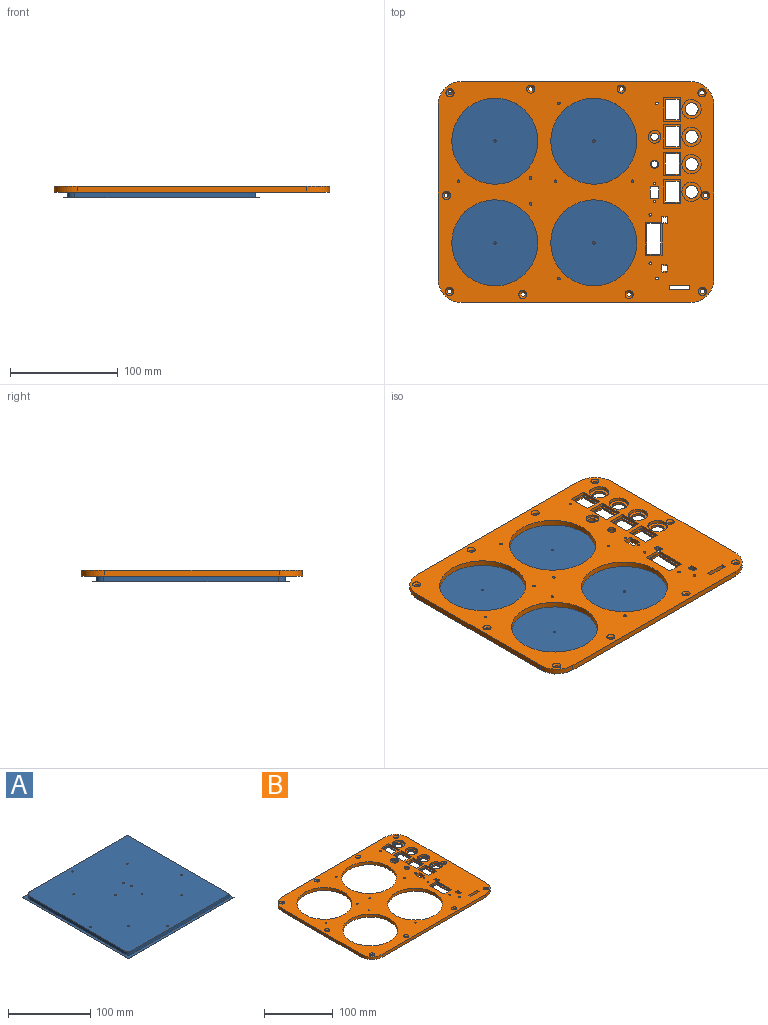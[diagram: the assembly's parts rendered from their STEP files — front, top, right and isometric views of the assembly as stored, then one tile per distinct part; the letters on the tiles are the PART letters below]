
ASSEMBLY  parts=2 mates=1
PART A: 37 faces, bbox 182.3x183x5.2 mm
  f0: plane 168.95x5.1mm, normal (0,1,0), area 861.6mm2, adj f2,f17,f18,f19
  f1: plane 163.3x5.1mm, normal (-1,0,0), area 832.8mm2, adj f16,f17,f18,f19
  f2: plane 176x5.1mm, normal (1,0,0), area 897.6mm2, adj f0,f15,f18,f19
  f3: cylinder r=1.19mm len=5.1mm, axis (0,0,1), area 38.2mm2, adj f18,f35
  f4: cylinder r=1.19mm len=5.1mm, axis (0,0,1), area 38.2mm2, adj f18,f34
  f5: cylinder r=1.19mm len=5.1mm, axis (0,0,1), area 38.2mm2, adj f18,f33
  f6: cylinder r=1.19mm len=5.1mm, axis (0,0,1), area 38.2mm2, adj f18,f32
  f7: cylinder r=1.19mm len=5.1mm, axis (0,0,1), area 38.2mm2, adj f18,f31
  f8: cylinder r=1.19mm len=5.1mm, axis (0,0,1), area 38.2mm2, adj f18,f30
  f9: cylinder r=1.19mm len=5.1mm, axis (0,0,1), area 38.2mm2, adj f18,f29
  f10: cylinder r=1.19mm len=5.1mm, axis (0,0,1), area 38.2mm2, adj f18,f28
  f11: cylinder r=1.19mm len=5.1mm, axis (0,0,1), area 38.2mm2, adj f18,f27
  f12: cylinder r=1.19mm len=5.1mm, axis (0,0,1), area 38.2mm2, adj f18,f26
  f13: cylinder r=1.19mm len=5.1mm, axis (0,0,1), area 38.2mm2, adj f18,f25
  f14: cylinder r=1.19mm len=5.1mm, axis (0,0,1), area 38.2mm2, adj f18,f24
  f15: plane 168.95x5.1mm, normal (0,-1,0), area 861.6mm2, adj f2,f16,f18,f19
  f16: cylinder r=6.35mm len=6.35mm, axis (0,0,-1), area 50.9mm2, adj f1,f15,f18,f19
  f17: cylinder r=6.35mm len=6.35mm, axis (0,0,1), area 50.9mm2, adj f0,f1,f18,f19
  f18: plane 176x175.3mm, normal (0,0,1), area 30782.1mm2, adj f0,f1,f2,f3,f4,f5,f6,f7
  f19: plane 183x182.3mm, normal (0,0,1), area 2525.4mm2, adj f0,f1,f2,f15,f16,f17,f20,f21
  f20: plane 182.3x0.1mm, normal (0,-1,0), area 18.2mm2, adj f19,f21,f23,f36
  f21: plane 183x0.1mm, normal (1,0,0), area 18.3mm2, adj f19,f20,f22,f36
  f22: plane 182.3x0.1mm, normal (0,1,0), area 18.2mm2, adj f19,f21,f23,f36
  f23: plane 183x0.1mm, normal (-1,0,0), area 18.3mm2, adj f19,f20,f22,f36
  f24: plane 2.38x2.38mm, normal (0,0,1), area 4.5mm2, adj f14
  f25: plane 2.38x2.38mm, normal (0,0,1), area 4.5mm2, adj f13
  f26: plane 2.38x2.38mm, normal (0,0,1), area 4.5mm2, adj f12
  f27: plane 2.38x2.38mm, normal (0,0,1), area 4.5mm2, adj f11
  f28: plane 2.38x2.38mm, normal (0,0,1), area 4.5mm2, adj f10
  f29: plane 2.38x2.38mm, normal (0,0,1), area 4.5mm2, adj f9
  f30: plane 2.38x2.38mm, normal (0,0,1), area 4.5mm2, adj f8
  f31: plane 2.38x2.38mm, normal (0,0,1), area 4.5mm2, adj f7
  f32: plane 2.38x2.38mm, normal (0,0,1), area 4.5mm2, adj f6
  f33: plane 2.38x2.38mm, normal (0,0,1), area 4.5mm2, adj f5
  f34: plane 2.38x2.38mm, normal (0,0,1), area 4.5mm2, adj f4
  f35: plane 2.38x2.38mm, normal (0,0,1), area 4.5mm2, adj f3
  f36: plane 183x182.3mm, normal (0,0,-1), area 33360.9mm2, adj f20,f21,f22,f23
PART B: 134 faces, bbox 256.4x205.6x5.2 mm
  f0: plane 256.41x205.61mm, normal (0,0,1), area 28460.5mm2, adj f25,f26,f32,f33,f34,f35,f36,f37
  f1: cylinder r=6mm len=12mm, axis (0,0,1), area 82.9mm2, adj f23,f132
  f2: plane 12.9x2.2mm, normal (0,-1,0), area 28.4mm2, adj f3,f5,f23,f131
  f3: plane 19.5x2.2mm, normal (1,0,0), area 42.9mm2, adj f2,f4,f23,f131
  f4: plane 12.9x2.2mm, normal (0,1,0), area 28.4mm2, adj f3,f5,f23,f131
  f5: plane 19.5x2.2mm, normal (-1,0,0), area 42.9mm2, adj f2,f4,f23,f131
  f6: plane 12.9x2.2mm, normal (0,-1,0), area 28.4mm2, adj f7,f9,f23,f126
  f7: plane 19.5x2.2mm, normal (1,0,0), area 42.9mm2, adj f6,f8,f23,f126
  f8: plane 12.9x2.2mm, normal (0,1,0), area 28.4mm2, adj f7,f9,f23,f126
  f9: plane 19.5x2.2mm, normal (-1,0,0), area 42.9mm2, adj f6,f8,f23,f126
  f10: plane 12.9x2.2mm, normal (0,-1,0), area 28.4mm2, adj f11,f13,f23,f121
  f11: plane 19.5x2.2mm, normal (1,0,0), area 42.9mm2, adj f10,f12,f23,f121
  f12: plane 12.9x2.2mm, normal (0,1,0), area 28.4mm2, adj f11,f13,f23,f121
  f13: plane 19.5x2.2mm, normal (-1,0,0), area 42.9mm2, adj f10,f12,f23,f121
  f14: cylinder r=6mm len=12mm, axis (0,0,1), area 82.9mm2, adj f23,f115
  f15: cylinder r=6mm len=12mm, axis (0,0,1), area 82.9mm2, adj f23,f113
  f16: cylinder r=6mm len=12mm, axis (0,0,1), area 82.9mm2, adj f23,f111
  f17: plane 12.9x2.2mm, normal (0,-1,0), area 28.4mm2, adj f18,f20,f23,f110
  f18: plane 19.5x2.2mm, normal (1,0,0), area 42.9mm2, adj f17,f19,f23,f110
  f19: plane 12.9x2.2mm, normal (0,1,0), area 28.4mm2, adj f18,f20,f23,f110
  f20: plane 19.5x2.2mm, normal (-1,0,0), area 42.9mm2, adj f17,f19,f23,f110
  f21: cylinder r=3.2mm len=6.4mm, axis (0,0,1), area 60.3mm2, adj f23,f104
  f22: cylinder r=3.5mm len=7mm, axis (0,0,1), area 66mm2, adj f23,f102
  f23: plane 256.41x205.61mm, normal (0,0,-1), area 29890.9mm2, adj f1,f2,f3,f4,f5,f6,f7,f8
  f24: plane 30.5x15.6mm, normal (0,0,1), area 106.7mm2, adj f25,f26,f94,f95,f96,f97,f98,f99
  f25: plane 5.2x5mm, normal (1,0,0), area 25.4mm2, adj f0,f23,f24,f26,f72,f94
  f26: cylinder r=1mm len=5.2mm, axis (0,0,1), area 13.2mm2, adj f0,f23,f24,f25,f73,f95
  f27: cylinder r=2.15mm len=4.3mm, axis (0,0,-1), area 45mm2, adj f23,f45
  f28: cylinder r=2.15mm len=4.3mm, axis (0,0,-1), area 45mm2, adj f23,f54
  f29: cylinder r=2.15mm len=4.3mm, axis (0,0,-1), area 45mm2, adj f23,f53
  f30: cylinder r=2.15mm len=4.3mm, axis (0,0,-1), area 45mm2, adj f23,f52
  f31: cylinder r=2.15mm len=4.3mm, axis (0,0,-1), area 45mm2, adj f23,f51
  f32: plane 213.51x5.2mm, normal (0,1,0), area 1110.3mm2, adj f0,f23,f33,f44
  f33: cylinder r=21.45mm len=21.45mm, axis (0,0,-1), area 175.2mm2, adj f0,f23,f32,f34
  f34: plane 162.71x5.2mm, normal (-1,0,0), area 846.1mm2, adj f0,f23,f33,f35
  f35: cylinder r=21.45mm len=21.45mm, axis (0,0,-1), area 175.2mm2, adj f0,f23,f34,f36
  f36: plane 213.51x5.2mm, normal (0,-1,0), area 1110.3mm2, adj f0,f23,f35,f37
  f37: cylinder r=21.45mm len=21.45mm, axis (0,0,-1), area 175.2mm2, adj f0,f23,f36,f38
  f38: plane 162.71x5.2mm, normal (1,0,0), area 846.1mm2, adj f0,f23,f37,f44
  f39: cylinder r=2.15mm len=4.3mm, axis (0,0,-1), area 45mm2, adj f23,f48
  f40: cylinder r=2.15mm len=4.3mm, axis (0,0,-1), area 45mm2, adj f23,f50
  f41: cylinder r=2.15mm len=4.3mm, axis (0,0,-1), area 45mm2, adj f23,f46
  f42: cylinder r=2.15mm len=4.3mm, axis (0,0,-1), area 45mm2, adj f23,f49
  f43: cylinder r=2.15mm len=4.3mm, axis (0,0,-1), area 45mm2, adj f23,f47
  f44: cylinder r=21.45mm len=21.45mm, axis (0,0,-1), area 175.2mm2, adj f0,f23,f32,f38
  f45: cone r=3.77mm half-angle=41deg, axis (0,0,1), area 46mm2, adj f0,f27
  f46: cone r=3.77mm half-angle=41deg, axis (0,0,1), area 46mm2, adj f0,f41
  f47: cone r=3.77mm half-angle=41deg, axis (0,0,1), area 46mm2, adj f0,f43
  f48: cone r=3.77mm half-angle=41deg, axis (0,0,1), area 46mm2, adj f0,f39
  f49: cone r=3.77mm half-angle=41deg, axis (0,0,1), area 46mm2, adj f0,f42
  f50: cone r=3.77mm half-angle=41deg, axis (0,0,1), area 46mm2, adj f0,f40
  f51: cone r=3.77mm half-angle=41deg, axis (0,0,1), area 46mm2, adj f0,f31
  f52: cone r=3.77mm half-angle=41deg, axis (0,0,1), area 46mm2, adj f0,f30
  f53: cone r=3.77mm half-angle=41deg, axis (0,0,1), area 46mm2, adj f0,f29
  f54: cone r=3.77mm half-angle=41deg, axis (0,0,1), area 46mm2, adj f0,f28
  f55: cylinder r=40mm len=80mm, axis (0,0,1), area 1306.9mm2, adj f0,f23
  f56: cylinder r=40mm len=80mm, axis (0,0,1), area 1306.9mm2, adj f0,f23
  f57: cylinder r=40mm len=80mm, axis (0,0,1), area 1306.9mm2, adj f0,f23
  f58: cylinder r=40mm len=80mm, axis (0,0,1), area 1306.9mm2, adj f0,f23
  f59: cylinder r=1.19mm len=5.2mm, axis (0,0,1), area 38.9mm2, adj f0,f23
  f60: cylinder r=1.19mm len=5.2mm, axis (0,0,1), area 38.9mm2, adj f0,f23
  f61: cylinder r=1.19mm len=5.2mm, axis (0,0,1), area 38.9mm2, adj f0,f23
  f62: cylinder r=1.19mm len=5.2mm, axis (0,0,1), area 38.9mm2, adj f0,f23
  f63: cylinder r=1.19mm len=5.2mm, axis (0,0,1), area 38.9mm2, adj f0,f23
  f64: cylinder r=1.19mm len=5.2mm, axis (0,0,1), area 38.9mm2, adj f0,f23
  f65: cylinder r=1.19mm len=5.2mm, axis (0,0,1), area 38.9mm2, adj f0,f23
  f66: cylinder r=1.19mm len=5.2mm, axis (0,0,1), area 38.9mm2, adj f0,f23
  f67: cylinder r=1.19mm len=5.2mm, axis (0,0,1), area 38.9mm2, adj f0,f23
  f68: cylinder r=1.19mm len=5.2mm, axis (0,0,1), area 38.9mm2, adj f0,f23
  f69: cylinder r=1.19mm len=5.2mm, axis (0,0,1), area 38.9mm2, adj f0,f23
  f70: cylinder r=1mm len=5.2mm, axis (0,0,1), area 16.3mm2, adj f0,f23,f71,f75
  f71: plane 5.2x1.3mm, normal (0,-1,0), area 6.8mm2, adj f0,f23,f70,f72
  f72: cylinder r=1mm len=5.2mm, axis (0,0,1), area 16.3mm2, adj f0,f23,f25,f71
  f73: plane 5.2x1.3mm, normal (0,1,0), area 6.8mm2, adj f0,f23,f26,f74
  f74: cylinder r=1mm len=5.2mm, axis (0,0,1), area 16.3mm2, adj f0,f23,f73,f75
  f75: plane 5.2x5mm, normal (-1,0,0), area 26mm2, adj f0,f23,f70,f74
  f76: cylinder r=1mm len=5.2mm, axis (0,0,1), area 16.3mm2, adj f0,f23,f77,f83
  f77: plane 5.2x5mm, normal (1,0,0), area 26mm2, adj f0,f23,f76,f78
  f78: cylinder r=1mm len=5.2mm, axis (0,0,1), area 16.3mm2, adj f0,f23,f77,f79
  f79: plane 5.2x1.3mm, normal (0,1,0), area 6.8mm2, adj f0,f23,f78,f80
  f80: cylinder r=1mm len=5.2mm, axis (0,0,1), area 16.3mm2, adj f0,f23,f79,f81
  f81: plane 5.2x5mm, normal (-1,0,0), area 26mm2, adj f0,f23,f80,f82
  f82: cylinder r=1mm len=5.2mm, axis (0,0,1), area 16.3mm2, adj f0,f23,f81,f83
  f83: plane 5.2x1.3mm, normal (0,-1,0), area 6.8mm2, adj f0,f23,f76,f82
  f84: plane 19x5.2mm, normal (0,-1,0), area 98.8mm2, adj f0,f23,f85,f87
  f85: plane 5.2x4mm, normal (1,0,0), area 20.8mm2, adj f0,f23,f84,f86
  f86: plane 19x5.2mm, normal (0,1,0), area 98.8mm2, adj f0,f23,f85,f87
  f87: plane 5.2x4mm, normal (-1,0,0), area 20.8mm2, adj f0,f23,f84,f86
  f88: cylinder r=1.19mm len=5.2mm, axis (0,0,1), area 38.9mm2, adj f0,f23
  f89: plane 8x5.2mm, normal (0,-1,0), area 41.6mm2, adj f0,f23,f90,f92
  f90: plane 10.9x5.2mm, normal (1,0,0), area 56.7mm2, adj f0,f23,f89,f91
  f91: plane 8x5.2mm, normal (0,1,0), area 41.6mm2, adj f0,f23,f90,f92
  f92: plane 10.9x5.2mm, normal (-1,0,0), area 56.7mm2, adj f0,f23,f89,f91
  f93: cylinder r=1.19mm len=5.2mm, axis (0,0,1), area 38.9mm2, adj f0,f23
  f94: plane 15.1x3mm, normal (0,-1,0), area 45.3mm2, adj f0,f24,f25,f96
  f95: plane 29.43x3mm, normal (-1,0,0), area 88.3mm2, adj f0,f24,f26,f97
  f96: plane 30.5x3mm, normal (1,0,0), area 91.5mm2, adj f0,f24,f94,f97
  f97: plane 15.6x3mm, normal (0,1,0), area 46.8mm2, adj f0,f24,f95,f96
  f98: plane 12.8x2.2mm, normal (0,-1,0), area 28.2mm2, adj f23,f24,f99,f101
  f99: plane 28.8x2.2mm, normal (1,0,0), area 63.4mm2, adj f23,f24,f98,f100
  f100: plane 12.8x2.2mm, normal (0,1,0), area 28.2mm2, adj f23,f24,f99,f101
  f101: plane 28.8x2.2mm, normal (-1,0,0), area 63.4mm2, adj f23,f24,f98,f100
  f102: plane 12x12mm, normal (0,0,1), area 74.6mm2, adj f22,f103
  f103: cylinder r=6mm len=12mm, axis (0,0,1), area 82.9mm2, adj f0,f102
  f104: plane 7.5x7.5mm, normal (0,0,1), area 12mm2, adj f21,f105
  f105: cylinder r=3.75mm len=7.5mm, axis (0,0,1), area 51.8mm2, adj f0,f104
  f106: plane 16x3mm, normal (0,-1,0), area 48mm2, adj f0,f107,f109,f110
  f107: plane 21.5x3mm, normal (1,0,0), area 64.5mm2, adj f0,f106,f108,f110
  f108: plane 16x3mm, normal (0,1,0), area 48mm2, adj f0,f107,f109,f110
  f109: plane 21.5x3mm, normal (-1,0,0), area 64.5mm2, adj f0,f106,f108,f110
  f110: plane 21.5x16mm, normal (0,0,1), area 92.4mm2, adj f17,f18,f19,f20,f106,f107,f108,f109
  f111: plane 18x18mm, normal (0,0,1), area 141.4mm2, adj f16,f112
  f112: cylinder r=9mm len=18mm, axis (0,0,1), area 169.6mm2, adj f0,f111
  f113: plane 18x18mm, normal (0,0,1), area 141.4mm2, adj f15,f114
  f114: cylinder r=9mm len=18mm, axis (0,0,1), area 169.6mm2, adj f0,f113
  f115: plane 18x18mm, normal (0,0,1), area 141.4mm2, adj f14,f116
  f116: cylinder r=9mm len=18mm, axis (0,0,1), area 169.6mm2, adj f0,f115
  f117: plane 16x3mm, normal (0,-1,0), area 48mm2, adj f0,f118,f120,f121
  f118: plane 21.5x3mm, normal (1,0,0), area 64.5mm2, adj f0,f117,f119,f121
  f119: plane 16x3mm, normal (0,1,0), area 48mm2, adj f0,f118,f120,f121
  f120: plane 21.5x3mm, normal (-1,0,0), area 64.5mm2, adj f0,f117,f119,f121
  f121: plane 21.5x16mm, normal (0,0,1), area 92.4mm2, adj f10,f11,f12,f13,f117,f118,f119,f120
  f122: plane 16x3mm, normal (0,-1,0), area 48mm2, adj f0,f123,f125,f126
  f123: plane 21.5x3mm, normal (1,0,0), area 64.5mm2, adj f0,f122,f124,f126
  f124: plane 16x3mm, normal (0,1,0), area 48mm2, adj f0,f123,f125,f126
  f125: plane 21.5x3mm, normal (-1,0,0), area 64.5mm2, adj f0,f122,f124,f126
  f126: plane 21.5x16mm, normal (0,0,1), area 92.4mm2, adj f6,f7,f8,f9,f122,f123,f124,f125
  f127: plane 16x3mm, normal (0,-1,0), area 48mm2, adj f0,f128,f130,f131
  f128: plane 21.5x3mm, normal (1,0,0), area 64.5mm2, adj f0,f127,f129,f131
  f129: plane 16x3mm, normal (0,1,0), area 48mm2, adj f0,f128,f130,f131
  f130: plane 21.5x3mm, normal (-1,0,0), area 64.5mm2, adj f0,f127,f129,f131
  f131: plane 21.5x16mm, normal (0,0,1), area 92.5mm2, adj f2,f3,f4,f5,f127,f128,f129,f130
  f132: plane 18x18mm, normal (0,0,1), area 141.4mm2, adj f1,f133
  f133: cylinder r=9mm len=18mm, axis (0,0,1), area 169.6mm2, adj f0,f132
PLACE A t=(-112.32,-92.52,-15.01)mm
PLACE B t=(-36.87,-45.21,-9.81)mm
MATE slider B.f55 <-> A.f3  axis (0,0,-1) through (-112.32,2.08,-9.81)mm
